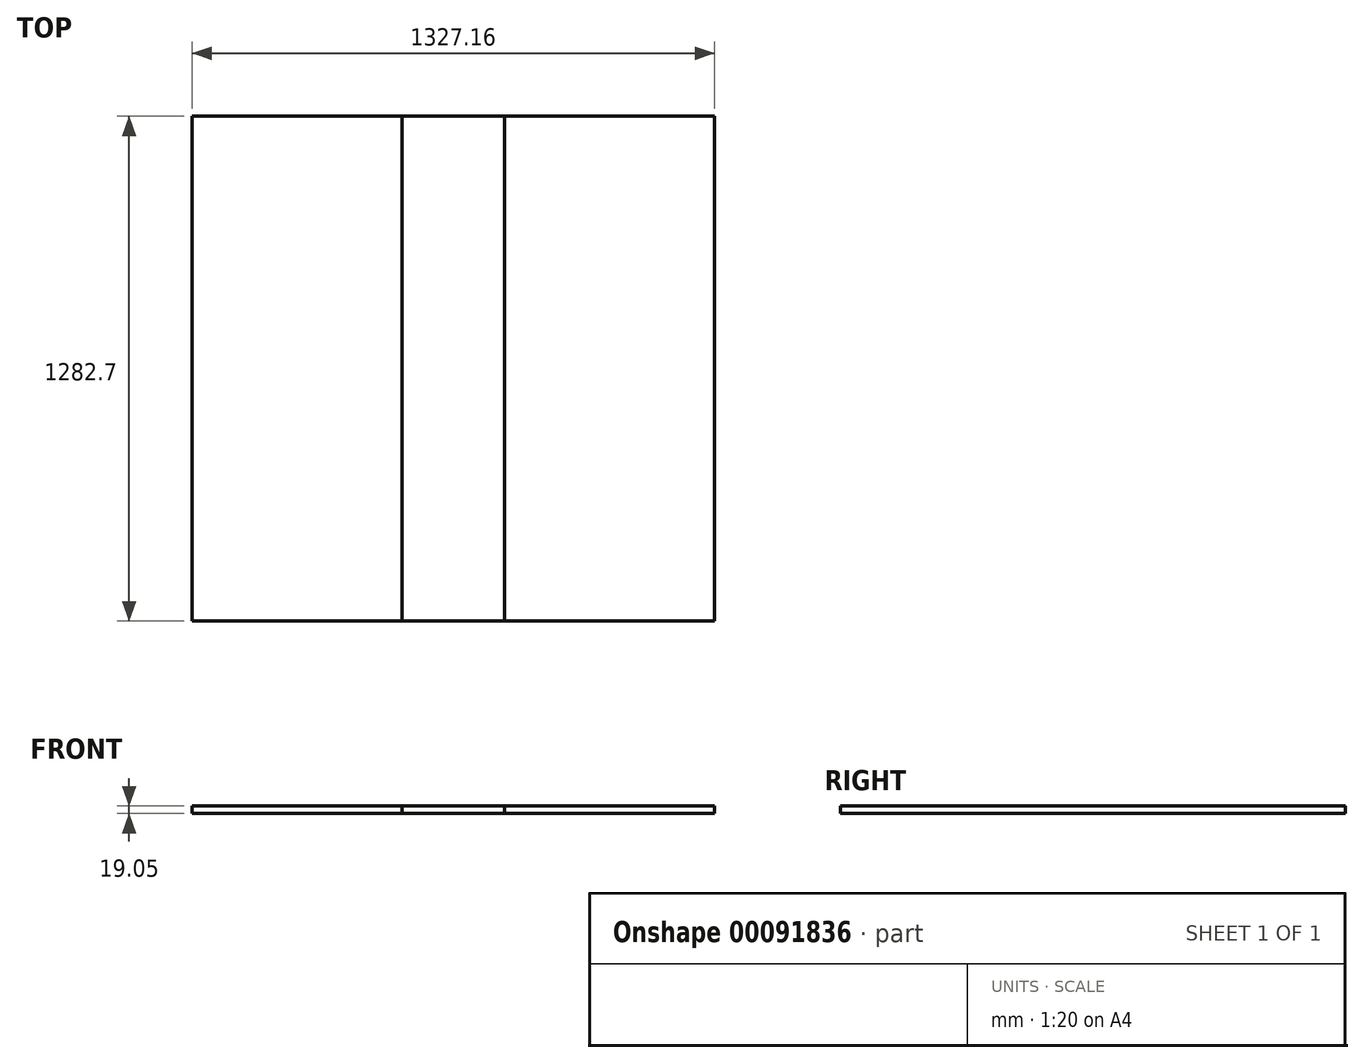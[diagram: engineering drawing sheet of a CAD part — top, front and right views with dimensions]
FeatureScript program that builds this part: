
annotation { "Feature Type Name" : "Feature", "Feature Type Description" : "" }
export const myFeature = defineFeature(function(context is Context, id is Id, definition is map)
    precondition{}
    {
        {
            var Q0;
            Q0=qCreatedBy(makeId("Top.planeOp"),FACE);
            var sketch = newSketch(context, id + "F0", { "sketchPlane" : qUnion([Q0])});
            skLineSegment(sketch, "E0.bottom", {"start": v(130.18, -641.35) * mm, "end": v(-130.17, -641.35) * mm});
            skLineSegment(sketch, "E0.top", {"start": v(130.17, 641.35) * mm, "end": v(-130.18, 641.35) * mm});
            skLineSegment(sketch, "E0.left", {"start": v(130.18, -641.35) * mm, "end": v(130.17, 641.35) * mm});
            skLineSegment(sketch, "E0.right", {"start": v(-130.17, -641.35) * mm, "end": v(-130.18, 641.35) * mm});
            skPoint(sketch, "E0.middle", {"position": v(0, 0) * mm});
            skLineSegment(sketch, "E1.bottom", {"start": v(130.18, -641.35) * mm, "end": v(663.58, -641.35) * mm});
            skLineSegment(sketch, "E1.top", {"start": v(130.18, 641.35) * mm, "end": v(663.57, 641.35) * mm});
            skLineSegment(sketch, "E1.left", {"start": v(130.18, -641.35) * mm, "end": v(130.18, 641.35) * mm});
            skLineSegment(sketch, "E1.right", {"start": v(663.58, -641.35) * mm, "end": v(663.57, 641.35) * mm});
            skLineSegment(sketch, "E2.bottom", {"start": v(-130.17, -641.35) * mm, "end": v(-663.58, -641.35) * mm});
            skLineSegment(sketch, "E2.top", {"start": v(-130.17, 641.35) * mm, "end": v(-663.58, 641.35) * mm});
            skLineSegment(sketch, "E2.left", {"start": v(-130.17, -641.35) * mm, "end": v(-130.17, 641.35) * mm});
            skLineSegment(sketch, "E2.right", {"start": v(-663.58, -641.35) * mm, "end": v(-663.58, 641.35) * mm});
            skSolve(sketch);
        }
        {
            var Q0;
            Q0=makeQuery(id+"F0.imprint","IMPRINT",FACE,{"disambiguationData":[TD([[makeQuery(id+"F0.imprint","IMPRINT",EDGE,{"derivedFrom":sQuery(id+"F0.wireOp",EDGE,"E2.bottom")}),-1.0]])]});
            extrude(context, id + "F1", {"entities" : qUnion([Q0]), "depth" : 19.05 * mm});
        }
        {
            var Q0;
            Q0=makeQuery(id+"F0.imprint","IMPRINT",FACE,{"disambiguationData":[TD([[makeQuery(id+"F0.imprint","IMPRINT",EDGE,{"derivedFrom":sQuery(id+"F0.wireOp",EDGE,"E1.bottom")}),1.0]])]});
            extrude(context, id + "F2", {"entities" : qUnion([Q0]), "depth" : 19.05 * mm});
        }
        {
            var Q0;
            Q0=makeQuery(id+"F0.imprint","IMPRINT",FACE,{"disambiguationData":[TD([[makeQuery(id+"F0.imprint","IMPRINT",EDGE,{"derivedFrom":sQuery(id+"F0.wireOp",EDGE,"E0.bottom")}),-1.0]])]});
            extrude(context, id + "F3", {"entities" : qUnion([Q0]), "depth" : 19.05 * mm});
        }
    });
